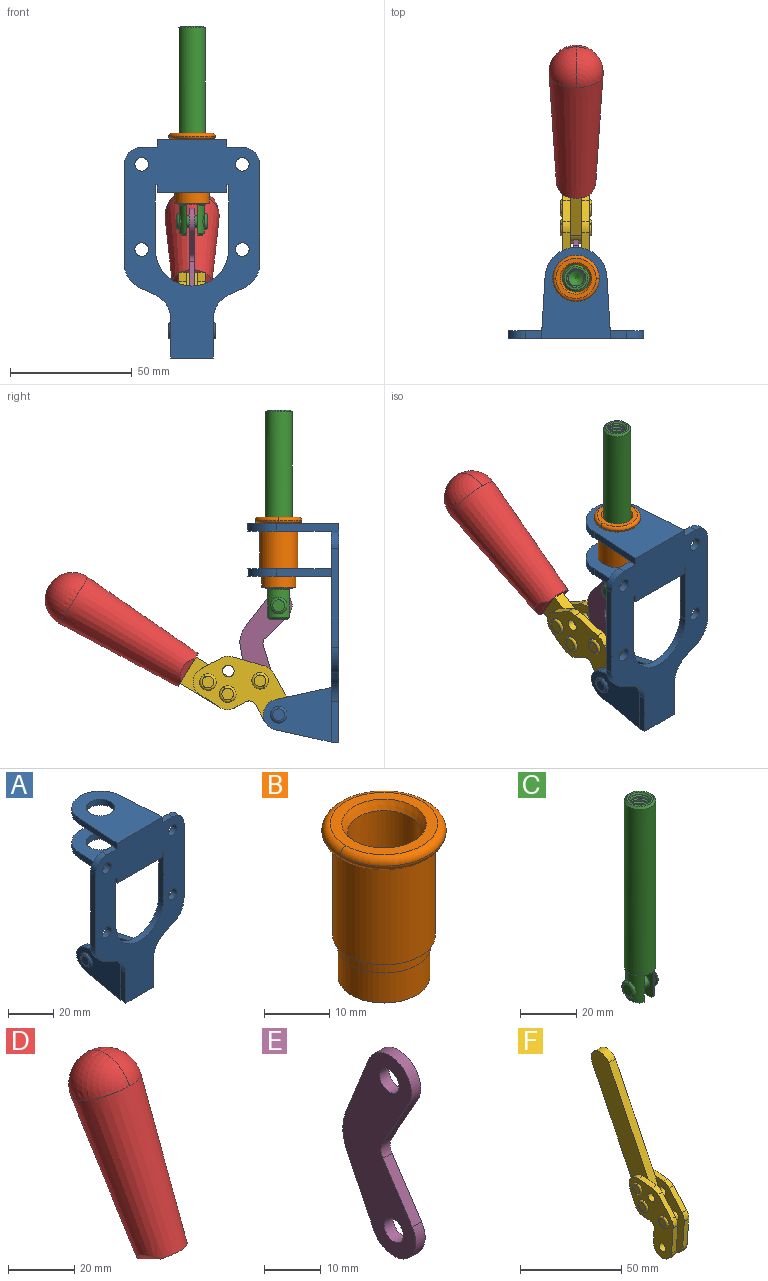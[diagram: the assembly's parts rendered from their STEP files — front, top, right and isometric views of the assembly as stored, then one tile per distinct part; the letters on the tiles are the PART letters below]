
ASSEMBLY  parts=6 mates=6
PART A: 55 faces, bbox 55.7x37.4x89.8 mm
  f0: torus R=2.41mm, axis (-1,0,0), area 15mm2, adj f11,f15,f25
  f1: torus R=2.41mm, axis (-1,0,0), area 15mm2, adj f10,f12,f22
  f2: cylinder r=2.78mm len=5.56mm, axis (0,-1,0), area 54.2mm2, adj f30,f54
  f3: cylinder r=14.99mm len=29.97mm, axis (0,-1,0), area 145.9mm2, adj f30,f49,f53,f54
  f4: cylinder r=2.78mm len=5.56mm, axis (0,-1,0), area 54.2mm2, adj f30,f54
  f5: cylinder r=2.78mm len=5.56mm, axis (0,-1,0), area 54.2mm2, adj f30,f54
  f6: cylinder r=2.78mm len=5.56mm, axis (0,-1,0), area 54.2mm2, adj f30,f54
  f7: cylinder r=6.35mm len=12.7mm, axis (0,0,1), area 123.6mm2, adj f27,f51
  f8: cylinder r=6.35mm len=12.7mm, axis (0,0,-1), area 124.7mm2, adj f21,f35
  f9: cylinder r=2.41mm len=11.18mm, axis (-1,0,0), area 169.4mm2, adj f16,f19
  f10: plane 4.83x4.83mm, normal (1,0,0), area 18.3mm2, adj f1,f12
  f11: plane 4.83x4.83mm, normal (-1,0,0), area 18.3mm2, adj f0,f15
  f12: torus R=2.41mm, axis (-1,0,0), area 15mm2, adj f1,f10,f22
  f13: cylinder r=6.35mm len=12.41mm, axis (1,0,0), area 53.4mm2, adj f18,f19,f22,f23
  f14: cylinder r=6.35mm len=12.41mm, axis (-1,0,0), area 53.4mm2, adj f16,f17,f24,f25
  f15: torus R=2.41mm, axis (-1,0,0), area 15mm2, adj f0,f11,f25
  f16: plane 27.86x22.35mm, normal (1,0,0), area 425.4mm2, adj f9,f14,f17,f24,f30
  f17: plane 22.86x4.97mm, normal (0,0.21,0.98), area 72.5mm2, adj f14,f16,f25,f30
  f18: plane 22.86x4.97mm, normal (0,0.21,0.98), area 72.5mm2, adj f13,f19,f22,f30
  f19: plane 27.86x22.35mm, normal (-1,0,0), area 425.4mm2, adj f9,f13,f18,f23,f30
  f20: cylinder r=12.7mm len=25.35mm, axis (0,0,-1), area 119.8mm2, adj f21,f34,f35,f36
  f21: plane 34.21x28.07mm, normal (0,0,-1), area 702.4mm2, adj f8,f20,f30,f34,f36
  f22: plane 27.96x22.45mm, normal (1,0,0), area 407.2mm2, adj f1,f12,f13,f18,f23,f30,f42,f43
  f23: plane 22.86x4.97mm, normal (0,0.21,-0.98), area 72.5mm2, adj f13,f19,f22,f44
  f24: plane 22.86x4.97mm, normal (0,0.21,-0.98), area 72.5mm2, adj f14,f16,f25,f44
  f25: plane 27.86x22.35mm, normal (-1,0,0), area 407.1mm2, adj f0,f14,f15,f17,f24,f30,f45,f46
  f26: plane 3.1x0.95mm, normal (0,0,-1), area 2.7mm2, adj f30,f49,f50,f54
  f27: plane 34.21x28.07mm, normal (0,0,1), area 702.4mm2, adj f7,f28,f30,f50,f52
  f28: cylinder r=12.7mm len=25.35mm, axis (0,0,1), area 118.8mm2, adj f27,f50,f51,f52
  f29: plane 3.1x0.95mm, normal (0,0,-1), area 2.7mm2, adj f30,f52,f53,f54
  f30: plane 86.54x55.63mm, normal (0,1,0), area 2362.9mm2, adj f2,f3,f4,f5,f6,f16,f17,f18
  f31: plane 40.56x3.1mm, normal (-1,0,0), area 125.7mm2, adj f30,f32,f48,f54
  f32: cylinder r=7.11mm len=7.11mm, axis (0,-1,0), area 34.6mm2, adj f30,f31,f33,f54
  f33: plane 6.67x3.1mm, normal (0,0,1), area 20.4mm2, adj f30,f32,f34,f54
  f34: plane 25.39x3.13mm, normal (-1,0.06,0), area 79.5mm2, adj f20,f21,f33,f35,f54
  f35: plane 37.31x28.45mm, normal (0,0,1), area 789.9mm2, adj f8,f20,f34,f36,f54
  f36: plane 25.39x3.13mm, normal (1,0.06,0), area 79.5mm2, adj f20,f21,f35,f37,f54
  f37: plane 6.67x3.1mm, normal (0,0,1), area 20.4mm2, adj f30,f36,f38,f54
  f38: cylinder r=7.11mm len=7.11mm, axis (0,-1,0), area 34.6mm2, adj f30,f37,f39,f54
  f39: plane 40.56x3.1mm, normal (1,0,0), area 125.7mm2, adj f30,f38,f40,f54
  f40: cylinder r=11.18mm len=10.16mm, axis (0,-1,0), area 39.5mm2, adj f30,f39,f41,f54
  f41: plane 6.09x3.1mm, normal (0.42,0,-0.91), area 20.8mm2, adj f30,f40,f42,f54
  f42: cylinder r=11.18mm len=9.41mm, axis (0,-1,0), area 37.2mm2, adj f22,f30,f41,f43,f54
  f43: plane 16.5x3.1mm, normal (1,0,0), area 51.1mm2, adj f22,f42,f44,f54
  f44: plane 17.37x3.1mm, normal (0,0,-1), area 53.8mm2, adj f23,f24,f30,f43,f45,f54
  f45: plane 16.5x3.1mm, normal (-1,0,0), area 51.1mm2, adj f25,f44,f46,f54
  f46: cylinder r=11.18mm len=9.41mm, axis (0,-1,0), area 37.2mm2, adj f25,f30,f45,f47,f54
  f47: plane 6.09x3.1mm, normal (-0.42,0,-0.91), area 20.8mm2, adj f30,f46,f48,f54
  f48: cylinder r=11.18mm len=10.16mm, axis (0,-1,0), area 39.5mm2, adj f30,f31,f47,f54
  f49: plane 26.54x3.1mm, normal (-1,0,0), area 82.3mm2, adj f3,f26,f30,f54
  f50: plane 25.39x3.1mm, normal (1,0.06,0), area 78.8mm2, adj f26,f27,f28,f51,f54
  f51: plane 37.31x28.45mm, normal (0,0,-1), area 789.9mm2, adj f7,f28,f50,f52,f54
  f52: plane 25.39x3.1mm, normal (-1,0.06,0), area 78.8mm2, adj f27,f28,f29,f51,f54
  f53: plane 26.54x3.1mm, normal (1,0,0), area 82.3mm2, adj f3,f29,f30,f54
  f54: plane 89.66x55.63mm, normal (0,-1,0), area 2678.5mm2, adj f2,f3,f4,f5,f6,f26,f29,f31
PART B: 15 faces, bbox 20.6x20.6x28.7 mm
  f0: torus R=8.26mm, axis (0,0,1), area 56.8mm2, adj f1,f10,f12
  f1: torus R=8.26mm, axis (0,0,1), area 56.8mm2, adj f0,f6,f13
  f2: cylinder r=5.59mm len=25.91mm, axis (0,0,1), area 909.6mm2, adj f3,f4
  f3: cone r=6.86mm half-angle=45deg, axis (0,0,-1), area 70.2mm2, adj f2,f14
  f4: cone r=6.47mm half-angle=30deg, axis (0,0,1), area 66.7mm2, adj f2,f13
  f5: cylinder r=7.04mm len=14.07mm, axis (0,0,1), area 252.6mm2, adj f11,f14
  f6: torus R=8.26mm, axis (0,0,1), area 56.8mm2, adj f1,f12,f13
  f7: cylinder r=7.16mm len=14.33mm, axis (0,0,1), area 91.5mm2, adj f9,f11
  f8: cylinder r=7.86mm len=18.42mm, axis (0,0,1), area 909.6mm2, adj f9,f10
  f9: plane 15.72x15.72mm, normal (0,0,-1), area 33mm2, adj f7,f8
  f10: plane 16.51x16.51mm, normal (0,0,-1), area 19.9mm2, adj f0,f8,f12
  f11: plane 14.33x14.33mm, normal (0,0,-1), area 5.7mm2, adj f5,f7
  f12: torus R=8.26mm, axis (0,0,1), area 56.8mm2, adj f0,f6,f10
  f13: plane 16.51x16.51mm, normal (0,0,1), area 82.7mm2, adj f1,f4,f6
  f14: plane 14.07x14.07mm, normal (0,0,-1), area 7.8mm2, adj f3,f5
PART C: 48 faces, bbox 12.6x11.1x86.1 mm
  f0: torus R=2.41mm, axis (-1,0,0), area 15mm2, adj f30,f32,f34
  f1: torus R=2.41mm, axis (-1,0,0), area 15mm2, adj f29,f31,f33
  f2: cylinder r=5.54mm len=72.39mm, axis (0,0,1), area 2518.5mm2, adj f3,f4,f42,f43
  f3: cone r=5.54mm half-angle=45deg, axis (0,0,1), area 7.6mm2, adj f2,f5,f41
  f4: cone r=5.54mm half-angle=45deg, axis (0,0,-1), area 34.9mm2, adj f2,f39
  f5: cylinder r=5.08mm len=11.48mm, axis (0,0,1), area 108.3mm2, adj f3,f7,f8,f41
  f6: cylinder r=2.41mm len=4.83mm, axis (-1,0,0), area 71.2mm2, adj f40,f41
  f7: cylinder r=2.41mm len=4.83mm, axis (-1,0,0), area 7.6mm2, adj f5,f34
  f8: cone r=5.08mm half-angle=45deg, axis (0,0,1), area 10.6mm2, adj f5,f37,f41
  f9: cone r=3.98mm half-angle=45deg, axis (0,0,1), area 17.6mm2, adj f27,f39,f45,f46,f47
  f10: cylinder r=2.41mm len=4.83mm, axis (-1,0,0), area 7.6mm2, adj f33,f38
  f11: cylinder r=3.2mm len=6.4mm, axis (0,0,1), area 78.4mm2, adj f12,f28,f44,f45,f47
  f12: cylinder r=3.2mm len=6.4mm, axis (0,0,1), area 10.5mm2, adj f11,f13,f45,f47
  f13: cylinder r=3.2mm len=6.4mm, axis (0,0,1), area 10.5mm2, adj f12,f14,f45,f47
  f14: cylinder r=3.2mm len=6.4mm, axis (0,0,1), area 10.5mm2, adj f13,f15,f45,f47
  f15: cylinder r=3.2mm len=6.4mm, axis (0,0,1), area 10.5mm2, adj f14,f16,f45,f47
  f16: cylinder r=3.2mm len=6.4mm, axis (0,0,1), area 10.5mm2, adj f15,f17,f45,f47
  f17: cylinder r=3.2mm len=6.4mm, axis (0,0,1), area 10.5mm2, adj f16,f18,f45,f47
  f18: cylinder r=3.2mm len=6.4mm, axis (0,0,1), area 10.5mm2, adj f17,f19,f45,f47
  f19: cylinder r=3.2mm len=6.4mm, axis (0,0,1), area 10.5mm2, adj f18,f20,f45,f47
  f20: cylinder r=3.2mm len=6.4mm, axis (0,0,1), area 10.5mm2, adj f19,f21,f45,f47
  f21: cylinder r=3.2mm len=6.4mm, axis (0,0,1), area 10.5mm2, adj f20,f22,f45,f47
  f22: cylinder r=3.2mm len=6.4mm, axis (0,0,1), area 10.5mm2, adj f21,f23,f45,f47
  f23: cylinder r=3.2mm len=6.4mm, axis (0,0,1), area 10.5mm2, adj f22,f24,f45,f47
  f24: cylinder r=3.2mm len=6.4mm, axis (0,0,1), area 10.5mm2, adj f23,f25,f45,f47
  f25: cylinder r=3.2mm len=6.4mm, axis (0,0,1), area 10.5mm2, adj f24,f26,f45,f47
  f26: cylinder r=3.2mm len=6.4mm, axis (0,0,1), area 10.5mm2, adj f25,f27,f45,f47
  f27: cylinder r=3.2mm len=6.4mm, axis (0,0,1), area 7.4mm2, adj f9,f26,f45,f47
  f28: cone r=3.2mm half-angle=60deg, axis (0,0,1), area 37.2mm2, adj f11
  f29: plane 4.83x4.83mm, normal (-1,0,0), area 18.3mm2, adj f1,f31
  f30: plane 4.83x4.83mm, normal (1,0,0), area 18.3mm2, adj f0,f32
  f31: torus R=2.41mm, axis (-1,0,0), area 15mm2, adj f1,f29,f33
  f32: torus R=2.41mm, axis (-1,0,0), area 15mm2, adj f0,f30,f34
  f33: plane 6.83x6.83mm, normal (1,0,0), area 18.3mm2, adj f1,f10,f31
  f34: plane 6.83x6.83mm, normal (-1,0,0), area 18.3mm2, adj f0,f7,f32
  f35: cone r=5.08mm half-angle=45deg, axis (0,0,1), area 10.6mm2, adj f36,f38,f40
  f36: plane 7.25x1.97mm, normal (0,0,-1), area 10mm2, adj f35,f40
  f37: plane 7.25x1.97mm, normal (0,0,-1), area 10mm2, adj f8,f41
  f38: cylinder r=5.08mm len=11.48mm, axis (0,0,1), area 108.3mm2, adj f10,f35,f40,f42
  f39: plane 9.55x9.55mm, normal (0,0,1), area 22mm2, adj f4,f9
  f40: plane 12.76x10.09mm, normal (1,0,0), area 95.7mm2, adj f6,f35,f36,f38,f42,f43
  f41: plane 12.76x10.09mm, normal (-1,0,0), area 95.7mm2, adj f3,f5,f6,f8,f37,f43
  f42: cone r=5.54mm half-angle=45deg, axis (0,0,1), area 7.6mm2, adj f2,f38,f40
  f43: plane 11.07x4.7mm, normal (0,0,-1), area 50.4mm2, adj f2,f40,f41
  f44: plane 0.89x0.62mm, normal (-1,0,0), area 0.3mm2, adj f11,f45,f46,f47
  f45: bspline ~24.8x7.63mm, area 266.6mm2, adj f9,f11,f12,f13,f14,f15,f16,f17
  f46: bspline ~24.87x7.63mm, area 73.6mm2, adj f9,f44,f45,f47
  f47: bspline ~24.98x7.63mm, area 272.5mm2, adj f9,f11,f12,f13,f14,f15,f16,f17
PART D: 11 faces, bbox 22.3x42.6x64.5 mm
  f0: sphere r=11.13mm, area 411.4mm2, adj f1,f8
  f1: cone r=11.11mm half-angle=3.3deg, axis (0,0.44,0.9), area 3251.8mm2, adj f0,f7,f8,f9,f10
  f2: cylinder r=6.16mm len=11.7mm, axis (1,0,0), area 89.5mm2, adj f3,f4,f5,f6
  f3: plane 60.23x36.75mm, normal (-1,0,0), area 763.6mm2, adj f2,f4,f6,f10
  f4: plane 51.37x25.05mm, normal (0,0.9,-0.44), area 264.2mm2, adj f2,f3,f5,f10
  f5: plane 60.23x36.75mm, normal (1,0,0), area 763.6mm2, adj f2,f4,f6,f10
  f6: plane 51.37x25.05mm, normal (0,-0.9,0.44), area 264.2mm2, adj f2,f3,f5,f10
  f7: plane 9.95x5.95mm, normal (0.71,-0.31,-0.64), area 25.8mm2, adj f1,f10
  f8: sphere r=11.13mm, area 411.4mm2, adj f0,f1
  f9: plane 9.95x5.95mm, normal (-0.71,-0.31,-0.64), area 25.8mm2, adj f1,f10
  f10: plane 14.27x11.38mm, normal (0,-0.44,-0.9), area 106.7mm2, adj f1,f3,f4,f5,f6,f7,f9
PART E: 12 faces, bbox 2.3x18.2x42.8 mm
  f0: cylinder r=2.4mm len=4.8mm, axis (1,0,0), area 34.9mm2, adj f4,f11
  f1: cylinder r=10.41mm len=8.47mm, axis (1,0,0), area 20.2mm2, adj f4,f9,f10,f11
  f2: cylinder r=3.05mm len=3.16mm, axis (1,0,0), area 7.7mm2, adj f4,f6,f7,f11
  f3: cylinder r=2.4mm len=4.8mm, axis (1,0,0), area 34.9mm2, adj f4,f11
  f4: plane 42.81x18.23mm, normal (-1,0,0), area 414.1mm2, adj f0,f1,f2,f3,f5,f6,f7,f8
  f5: cylinder r=5.54mm len=10.67mm, axis (1,0,0), area 41.8mm2, adj f4,f6,f10,f11
  f6: plane 11.66x6.53mm, normal (0,-0.87,-0.49), area 30.9mm2, adj f2,f4,f5,f11
  f7: plane 11.17x7.33mm, normal (0,-0.84,0.55), area 30.9mm2, adj f2,f4,f8,f11
  f8: cylinder r=5.54mm len=10.51mm, axis (1,0,0), area 41.8mm2, adj f4,f7,f9,f11
  f9: plane 13.67x6.67mm, normal (0,0.9,-0.44), area 35.1mm2, adj f1,f4,f8,f11
  f10: plane 14.1x5.7mm, normal (0,0.93,0.37), area 35.1mm2, adj f1,f4,f5,f11
  f11: plane 42.81x18.23mm, normal (1,0,0), area 414.1mm2, adj f0,f1,f2,f3,f5,f6,f7,f8
PART F: 59 faces, bbox 12.9x60.2x99.6 mm
  f0: torus R=2.39mm, axis (-1,0,0), area 14.9mm2, adj f20,f43,f51
  f1: torus R=2.39mm, axis (-1,0,0), area 14.9mm2, adj f19,f42,f51
  f2: torus R=2.39mm, axis (-1,0,0), area 14.9mm2, adj f18,f35,f51
  f3: torus R=2.39mm, axis (-1,0,0), area 14.9mm2, adj f14,f17,f23
  f4: torus R=2.39mm, axis (-1,0,0), area 14.9mm2, adj f13,f16,f23
  f5: torus R=2.39mm, axis (-1,0,0), area 14.9mm2, adj f12,f15,f23
  f6: cylinder r=2.39mm len=4.78mm, axis (1,0,0), area 46.5mm2, adj f48,f50,f51
  f7: cylinder r=2.39mm len=4.78mm, axis (1,0,0), area 46.5mm2, adj f50,f51
  f8: cylinder r=6.35mm len=12.68mm, axis (1,0,0), area 61.8mm2, adj f38,f39,f50,f51
  f9: cylinder r=2.39mm len=4.78mm, axis (-1,0,0), area 70.5mm2, adj f46,f50
  f10: cylinder r=2.39mm len=4.78mm, axis (-1,0,0), area 46.5mm2, adj f23,f45,f46
  f11: cylinder r=2.39mm len=4.78mm, axis (-1,0,0), area 46.5mm2, adj f23,f46
  f12: plane 4.78x4.78mm, normal (1,0,0), area 17.9mm2, adj f5,f15
  f13: plane 4.78x4.78mm, normal (1,0,0), area 17.9mm2, adj f4,f16
  f14: plane 4.78x4.78mm, normal (1,0,0), area 17.9mm2, adj f3,f17
  f15: torus R=2.39mm, axis (-1,0,0), area 14.9mm2, adj f5,f12,f23
  f16: torus R=2.39mm, axis (-1,0,0), area 14.9mm2, adj f4,f13,f23
  f17: torus R=2.39mm, axis (-1,0,0), area 14.9mm2, adj f3,f14,f23
  f18: plane 4.78x4.78mm, normal (-1,0,0), area 17.9mm2, adj f2,f35
  f19: plane 4.78x4.78mm, normal (-1,0,0), area 17.9mm2, adj f1,f42
  f20: plane 4.78x4.78mm, normal (-1,0,0), area 17.9mm2, adj f0,f43
  f21: plane 2.26x0.2mm, normal (1,0,0), area 0.2mm2, adj f31,f44
  f22: plane 2.26x0.2mm, normal (-1,0,0), area 0.2mm2, adj f41,f44
  f23: plane 39.37x30.77mm, normal (1,0,0), area 565.5mm2, adj f3,f4,f5,f10,f11,f15,f16,f17
  f24: cylinder r=6.1mm len=4.15mm, axis (-1,0,0), area 14.7mm2, adj f23,f25,f32,f46
  f25: plane 10.25x9.01mm, normal (0,-0.75,0.66), area 42.3mm2, adj f23,f24,f26,f46
  f26: cylinder r=6.35mm len=4.64mm, axis (-1,0,0), area 15.6mm2, adj f23,f25,f27,f46
  f27: plane 15.84x3.1mm, normal (0,-1,-0.07), area 49.2mm2, adj f23,f26,f28,f46
  f28: cylinder r=6.35mm len=12.68mm, axis (-1,0,0), area 61.8mm2, adj f23,f27,f29,f46
  f29: plane 8.11x3.1mm, normal (0,1,0.07), area 25.2mm2, adj f23,f28,f30,f46
  f30: cylinder r=3.05mm len=3.25mm, axis (-1,0,0), area 14.8mm2, adj f23,f29,f31,f46
  f31: plane 5.99x3.1mm, normal (0,0.07,-1), area 18.6mm2, adj f21,f23,f30,f44,f46
  f32: plane 9.5x3.1mm, normal (0,-0.07,1), area 29.5mm2, adj f23,f24,f33,f46,f47
  f33: cylinder r=6.1mm len=8.63mm, axis (-1,0,0), area 39.1mm2, adj f23,f32,f34,f47
  f34: plane 8.65x3.96mm, normal (0,0.91,-0.42), area 29.5mm2, adj f23,f33,f44,f47
  f35: torus R=2.39mm, axis (-1,0,0), area 14.9mm2, adj f2,f18,f51
  f36: plane 10.25x9.01mm, normal (0,-0.75,0.66), area 42.3mm2, adj f37,f49,f50,f51
  f37: cylinder r=6.35mm len=4.64mm, axis (1,0,0), area 15.6mm2, adj f36,f38,f50,f51
  f38: plane 15.84x3.1mm, normal (0,-1,-0.07), area 49.2mm2, adj f8,f37,f50,f51
  f39: plane 8.11x3.1mm, normal (0,1,0.07), area 25.2mm2, adj f8,f40,f50,f51
  f40: cylinder r=3.05mm len=3.25mm, axis (1,0,0), area 14.8mm2, adj f39,f41,f50,f51
  f41: plane 5.99x3.1mm, normal (0,0.07,-1), area 18.6mm2, adj f22,f40,f44,f50,f51
  f42: torus R=2.39mm, axis (-1,0,0), area 14.9mm2, adj f1,f19,f51
  f43: torus R=2.39mm, axis (-1,0,0), area 14.9mm2, adj f0,f20,f51
  f44: cylinder r=6.35mm len=12.12mm, axis (-1,0,0), area 128.9mm2, adj f21,f22,f23,f31,f34,f41,f46,f47
  f45: plane 2.65x1.35mm, normal (1,0,0), area 1mm2, adj f10,f55
  f46: plane 39.08x20.42mm, normal (-1,0,0), area 412.5mm2, adj f9,f10,f11,f24,f25,f26,f27,f28
  f47: plane 77.62x39.82mm, normal (1,0,0), area 850mm2, adj f32,f33,f34,f44,f53,f54,f55
  f48: plane 2.65x1.35mm, normal (-1,0,0), area 1mm2, adj f6,f55
  f49: cylinder r=6.1mm len=4.15mm, axis (1,0,0), area 14.7mm2, adj f36,f50,f51,f56
  f50: plane 39.08x20.42mm, normal (1,0,0), area 412.5mm2, adj f6,f7,f8,f9,f36,f37,f38,f39
  f51: plane 39.37x30.77mm, normal (-1,0,0), area 565.5mm2, adj f0,f1,f2,f6,f7,f8,f35,f36
  f52: plane 8.65x3.96mm, normal (0,0.91,-0.42), area 29.5mm2, adj f44,f51,f57,f58
  f53: plane 68.49x33.4mm, normal (0,0.9,-0.44), area 358.1mm2, adj f44,f47,f54,f58
  f54: cylinder r=6.35mm len=12.06mm, axis (1,0,0), area 93.7mm2, adj f47,f53,f55,f58
  f55: plane 68.49x33.4mm, normal (0,-0.9,0.44), area 358.1mm2, adj f44,f45,f46,f47,f48,f50,f54,f58
  f56: plane 9.5x3.1mm, normal (0,-0.07,1), area 29.5mm2, adj f49,f50,f51,f57,f58
  f57: cylinder r=6.1mm len=8.63mm, axis (1,0,0), area 39.1mm2, adj f51,f52,f56,f58
  f58: plane 77.62x39.82mm, normal (-1,0,0), area 850mm2, adj f44,f52,f53,f54,f55,f56,f57
PLACE A t=(-3.21,-3.03,-28.91)mm fixed
PLACE B t=(-3.21,-3.03,-28.91)mm
PLACE C t=(-3.21,-3.03,-31.72)mm
PLACE D rot(axis=(-1,0,0),32.7deg) t=(-3.18,18.18,-20.7)mm
PLACE E rot(axis=(1,0,0),15.9deg) t=(-3.21,2.14,-37.87)mm
PLACE F rot(axis=(-1,0,0),32.7deg) t=(-3.21,18.18,-20.7)mm
MATE revolute E.f3 <-> F.f4  axis (1,0,0) through (-3.21,29.2,-47.07)mm
MATE revolute E.f5 <-> C.f6  axis (1,0,0) through (-3.21,21.58,-16.25)mm
MATE fastened D.f2 <-> F.f54  axis (-1,0,0) through (-0.87,107.55,-12.94)mm
MATE revolute F.f7 <-> A.f0  axis (-1,0,0) through (-3.21,21.58,-61)mm
MATE fastened B.f2 <-> A.f7  axis (0,0,-1) through (-3.21,21.58,17.48)mm
MATE slider C.f2 <-> A.f7  axis (0,0,1) through (-3.21,21.58,27.06)mm
